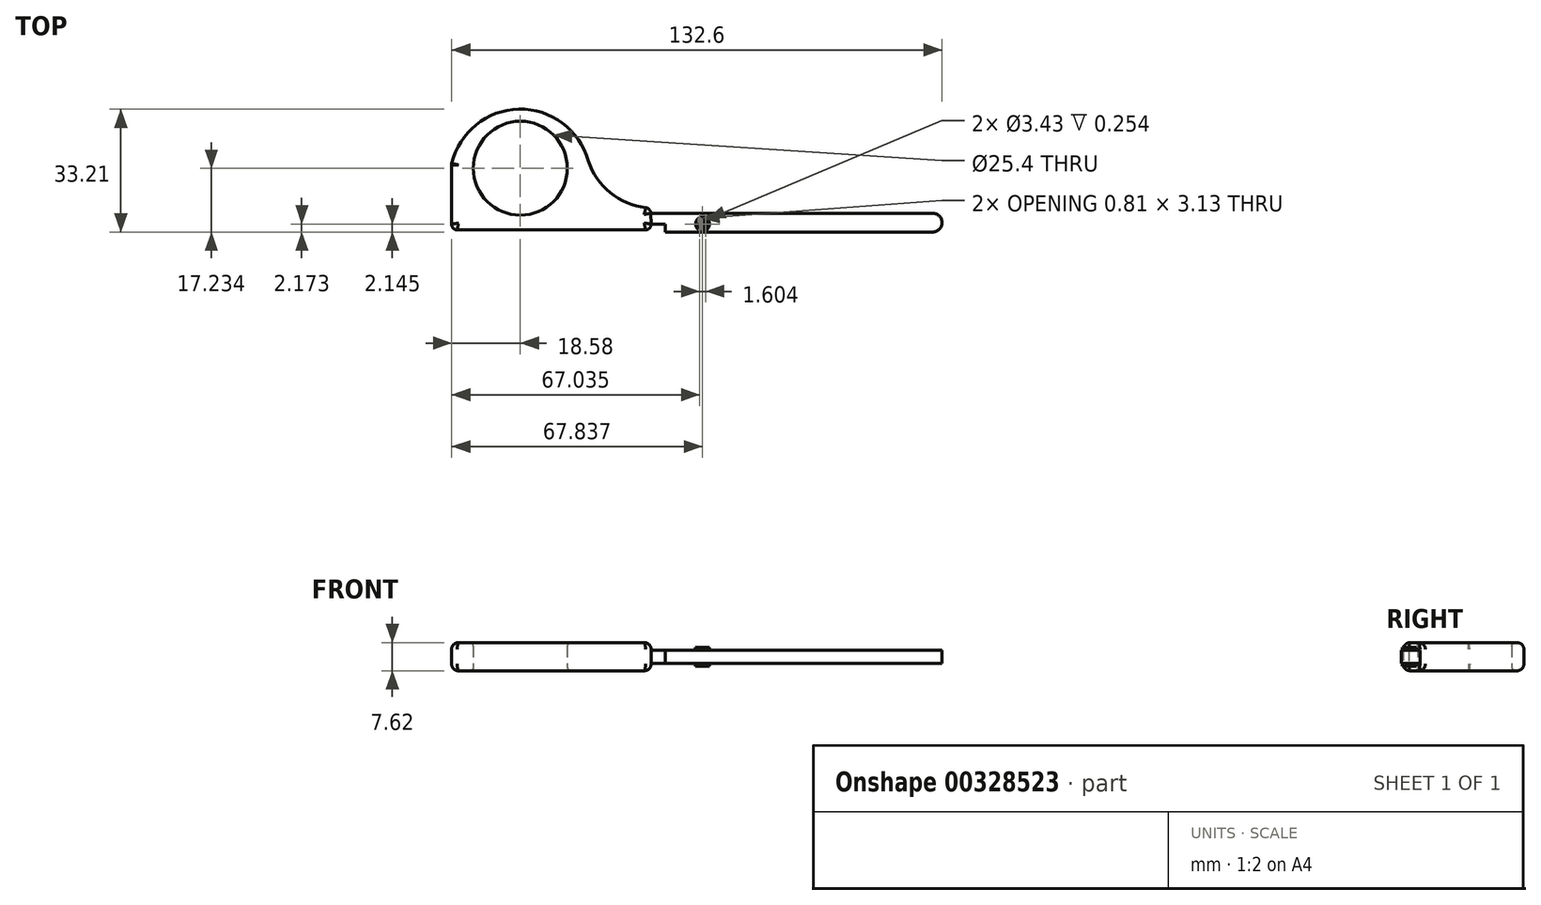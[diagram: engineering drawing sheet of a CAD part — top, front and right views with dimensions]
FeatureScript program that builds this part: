
annotation { "Feature Type Name" : "Feature", "Feature Type Description" : "" }
export const myFeature = defineFeature(function(context is Context, id is Id, definition is map)
    precondition{}
    {
        {
            var Q0;
            Q0=qCreatedBy(makeId("Top.planeOp"),FACE);
            var sketch = newSketch(context, id + "F0", { "sketchPlane" : qUnion([Q0])});
            skLineSegment(sketch, "E0", {"start": v(-56.25, 0) * mm, "end": v(-5.36, 0) * mm});
            skLineSegment(sketch, "E1", {"start": v(-57.77, 1.52) * mm, "end": v(-57.77, 17.6) * mm});
            skArc(sketch, "E2", {"start": v(-20.85, 18.71) * mm, "mid": v(-39.58, 32.62) * mm, "end": v(-57.73, 17.96) * mm});
            skArc(sketch, "E3", {"start": v(-20.82, 18.64) * mm, "mid": v(-14.89, 10.04) * mm, "end": v(-5.26, 5.97) * mm});
            skLineSegment(sketch, "E4", {"start": v(-3.91, 4.5) * mm, "end": v(-3.84, 1.56) * mm});
            skPoint(sketch, "E5.visualSharp", {"position": v(-3.95, 5.87) * mm});
            skArc(sketch, "E5.filletArc", {"start": v(-3.91, 4.5) * mm, "mid": v(-4.31, 5.49) * mm, "end": v(-5.26, 5.97) * mm});
            skPoint(sketch, "E6.visualSharp", {"position": v(-3.8, 0) * mm});
            skArc(sketch, "E6.filletArc", {"start": v(-5.36, 0) * mm, "mid": v(-4.27, 0.46) * mm, "end": v(-3.84, 1.56) * mm});
            skPoint(sketch, "E7.visualSharp", {"position": v(-57.77, 0) * mm});
            skArc(sketch, "E7.filletArc", {"start": v(-57.77, 1.52) * mm, "mid": v(-57.32, 0.45) * mm, "end": v(-56.25, 0) * mm});
            skPoint(sketch, "E8.visualSharp", {"position": v(-57.77, 17.78) * mm});
            skArc(sketch, "E8.filletArc", {"start": v(-57.73, 17.96) * mm, "mid": v(-57.76, 17.78) * mm, "end": v(-57.77, 17.6) * mm});
            skArc(sketch, "E9.filletArc", {"start": v(-20.85, 18.71) * mm, "mid": v(-20.84, 18.68) * mm, "end": v(-20.82, 18.64) * mm});
            skLineSegment(sketch, "E10", {"start": v(-3.91, 4.5) * mm, "end": v(72.29, 4.5) * mm});
            skLineSegment(sketch, "E11", {"start": v(-3.84, 1.56) * mm, "end": v(0, 1.56) * mm});
            skLineSegment(sketch, "E12", {"start": v(0, 1.56) * mm, "end": v(0, -0.58) * mm});
            skLineSegment(sketch, "E13", {"start": v(0, -0.58) * mm, "end": v(72.29, -0.58) * mm});
            skArc(sketch, "E14", {"start": v(72.29, -0.58) * mm, "mid": v(74.83, 1.96) * mm, "end": v(72.29, 4.5) * mm});
            skCircle(sketch, "E15", {"center": v(10.1, 1.56) * mm, "radius": 1.71 * mm});
            skCircle(sketch, "E16", {"center": v(-39.19, 16.65) * mm, "radius": 12.7 * mm});
            skSolve(sketch);
        }
        {
            var Q0;
            Q0=makeQuery(id+"F0.imprint","IMPRINT",FACE,{"disambiguationData":[TD([[makeQuery(id+"F0.imprint","IMPRINT",EDGE,{"derivedFrom":sQuery(id+"F0.wireOp",EDGE,"E0")}),1.0]])]});
            extrude(context, id + "F1", {"entities" : qUnion([Q0]), "endBound" : BoundingType.SYMMETRIC, "depth" : 7.62 * mm});
        }
        {
            var Q0;
            Q0=makeQuery(id+"F0.imprint","IMPRINT",FACE,{"disambiguationData":[TD([[makeQuery(id+"F0.imprint","IMPRINT",EDGE,{"derivedFrom":sQuery(id+"F0.wireOp",EDGE,"E4")}),1.0]])]});
            extrude(context, id + "F2", {"entities" : qUnion([Q0]), "operationType" : NewBodyOperationType.ADD, "endBound" : BoundingType.SYMMETRIC, "depth" : 3.56 * mm});
        }
        {
            var Q0;
            Q0=makeQuery(id+"F1.opExtrude","CAP_EDGE",EDGE,{"disambiguationData":[OSD([sQuery(id+"F0.wireOp",EDGE,"E2")])],"isStart":false});
            var Q1;
            Q1=makeQuery(id+"F1.opExtrude","CAP_EDGE",EDGE,{"disambiguationData":[OSD([sQuery(id+"F0.wireOp",EDGE,"E2")])],"isStart":true});
            var Q2;
            Q2=makeQuery(id+"F1.opExtrude","CAP_EDGE",EDGE,{"disambiguationData":[OSD([sQuery(id+"F0.wireOp",EDGE,"E3")])],"isStart":false});
            var Q3;
            Q3=makeQuery(id+"F1.opExtrude","CAP_EDGE",EDGE,{"disambiguationData":[OSD([sQuery(id+"F0.wireOp",EDGE,"E3")])],"isStart":true});
            var Q4;
            Q4=makeQuery(id+"F1.opExtrude","CAP_EDGE",EDGE,{"disambiguationData":[OSD([sQuery(id+"F0.wireOp",EDGE,"E8.filletArc")])],"isStart":false});
            var Q5;
            Q5=makeQuery(id+"F1.opExtrude","CAP_EDGE",EDGE,{"disambiguationData":[OSD([sQuery(id+"F0.wireOp",EDGE,"E8.filletArc")])],"isStart":true});
            var Q6;
            Q6=makeQuery(id+"F1.opExtrude","CAP_EDGE",EDGE,{"disambiguationData":[OSD([sQuery(id+"F0.wireOp",EDGE,"E1")])],"isStart":true});
            var Q7;
            Q7=makeQuery(id+"F1.opExtrude","CAP_EDGE",EDGE,{"disambiguationData":[OSD([sQuery(id+"F0.wireOp",EDGE,"E1")])],"isStart":false});
            var Q8;
            Q8=makeQuery(id+"F1.opExtrude","CAP_EDGE",EDGE,{"disambiguationData":[OSD([sQuery(id+"F0.wireOp",EDGE,"E7.filletArc")])],"isStart":false});
            var Q9;
            Q9=makeQuery(id+"F1.opExtrude","CAP_EDGE",EDGE,{"disambiguationData":[OSD([sQuery(id+"F0.wireOp",EDGE,"E0")])],"isStart":false});
            var Q10;
            Q10=makeQuery(id+"F1.opExtrude","CAP_EDGE",EDGE,{"disambiguationData":[OSD([sQuery(id+"F0.wireOp",EDGE,"E7.filletArc")])],"isStart":true});
            var Q11;
            Q11=makeQuery(id+"F1.opExtrude","CAP_EDGE",EDGE,{"disambiguationData":[OSD([sQuery(id+"F0.wireOp",EDGE,"E0")])],"isStart":true});
            var Q12;
            Q12=makeQuery(id+"F1.opExtrude","CAP_EDGE",EDGE,{"disambiguationData":[OSD([sQuery(id+"F0.wireOp",EDGE,"MBKP8UZo-nLue-SihB-gih0-BUNX2vB4kbxo")])],"isStart":false});
            var Q13;
            Q13=makeQuery(id+"F1.opExtrude","CAP_EDGE",EDGE,{"disambiguationData":[OSD([sQuery(id+"F0.wireOp",EDGE,"MBKP8UZo-nLue-SihB-gih0-BUNX2vB4kbxo")])],"isStart":true});
            var Q14;
            Q14=makeQuery(id+"F1.opExtrude","CAP_EDGE",EDGE,{"disambiguationData":[OSD([sQuery(id+"F0.wireOp",EDGE,"E5.filletArc")])],"isStart":false});
            var Q15;
            Q15=makeQuery(id+"F1.opExtrude","CAP_EDGE",EDGE,{"disambiguationData":[OSD([sQuery(id+"F0.wireOp",EDGE,"E4")])],"isStart":false});
            var Q16;
            Q16=makeQuery(id+"F1.opExtrude","CAP_EDGE",EDGE,{"disambiguationData":[OSD([sQuery(id+"F0.wireOp",EDGE,"E6.filletArc")])],"isStart":false});
            var Q17;
            Q17=makeQuery(id+"F1.opExtrude","CAP_EDGE",EDGE,{"disambiguationData":[OSD([sQuery(id+"F0.wireOp",EDGE,"E4")])],"isStart":true});
            var Q18;
            Q18=makeQuery(id+"F1.opExtrude","CAP_EDGE",EDGE,{"disambiguationData":[OSD([sQuery(id+"F0.wireOp",EDGE,"E6.filletArc")])],"isStart":true});
            var Q19;
            Q19=makeQuery(id+"F1.opExtrude","CAP_EDGE",EDGE,{"disambiguationData":[OSD([sQuery(id+"F0.wireOp",EDGE,"E5.filletArc")])],"isStart":true});
            fillet(context, id + "F3", {"entities" : qUnion([Q0, Q1, Q2, Q3, Q4, Q5, Q6, Q7, Q8, Q9, Q10, Q11, Q12, Q13, Q14, Q15, Q16, Q17, Q18, Q19]), "radius" : 1.84 * mm, "tangentPropagation" : true, "allowEdgeOverflow" : false});
        }
        {
            var Q0;
            Q0=makeQuery(id+"F1.opExtrude","CAP_EDGE",EDGE,{"disambiguationData":[OSD([sQuery(id+"F0.wireOp",EDGE,"E16")])],"isStart":true});
            var Q1;
            Q1=makeQuery(id+"F1.opExtrude","CAP_EDGE",EDGE,{"disambiguationData":[OSD([sQuery(id+"F0.wireOp",EDGE,"E16")])],"isStart":false});
            fillet(context, id + "F4", {"entities" : qUnion([Q0, Q1]), "radius" : 0.98 * mm, "tangentPropagation" : true, "allowEdgeOverflow" : false});
        }
        {
            var Q0;
            Q0=qCreatedBy(makeId("Top.planeOp"),FACE);
            var sketch = newSketch(context, id + "F5", { "sketchPlane" : qUnion([Q0])});
            skCircle(sketch, "E17", {"center": v(10.07, 1.6) * mm, "radius": 1.71 * mm});
            skLineSegment(sketch, "E18", {"start": v(9.67, 3.13) * mm, "end": v(9.67, 0) * mm});
            skLineSegment(sketch, "E19", {"start": v(10.07, 1.6) * mm, "end": v(10.07, -15.89) * mm, "construction": true});
            skLineSegment(sketch, "E20", {"start": v(10.07, -15.89) * mm, "end": v(10.07, 1.6) * mm, "construction": true});
            skLineSegment(sketch, "E21", {"start": v(10.07, 1.6) * mm, "end": v(10.07, 12.33) * mm, "construction": true});
            skLineSegment(sketch, "E22.MirrorCS", {"start": v(10.46, 3.13) * mm, "end": v(10.46, 0) * mm});
            skArc(sketch, "E23", {"start": v(9.67, 3.13) * mm, "mid": v(8.86, 1.56) * mm, "end": v(9.67, 0) * mm});
            skArc(sketch, "E24.MirrorCS", {"start": v(10.46, 3.13) * mm, "mid": v(11.27, 1.56) * mm, "end": v(10.46, 0) * mm});
            skCircle(sketch, "E25", {"center": v(10.07, 1.6) * mm, "radius": 1.89 * mm});
            skSolve(sketch);
        }
        {
            var Q0;
            Q0=makeQuery(id+"F5.imprint","IMPRINT",FACE,{"disambiguationData":[TD([[makeQuery(id+"F5.imprint","IMPRINT",EDGE,{"derivedFrom":sQuery(id+"F5.wireOp",EDGE,"E17")}),1.0]])]});
            extrude(context, id + "F6", {"entities" : qUnion([Q0]), "operationType" : NewBodyOperationType.ADD, "endBound" : BoundingType.SYMMETRIC, "depth" : 4.57 * mm});
        }
        {
            var Q0;
            Q0=makeQuery(id+"F5.imprint","IMPRINT",FACE,{"disambiguationData":[TD([[makeQuery(id+"F5.imprint","IMPRINT",EDGE,{"derivedFrom":sQuery(id+"F5.wireOp",EDGE,"E18")}),-1.0]])]});
            var Q1;
            Q1=makeQuery(id+"F5.imprint","IMPRINT",FACE,{"disambiguationData":[TD([[makeQuery(id+"F5.imprint","IMPRINT",EDGE,{"derivedFrom":sQuery(id+"F5.wireOp",EDGE,"E22.MirrorCS")}),1.0]])]});
            extrude(context, id + "F7", {"entities" : qUnion([Q0, Q1]), "operationType" : NewBodyOperationType.ADD, "endBound" : BoundingType.SYMMETRIC, "depth" : 4.95 * mm});
        }
        {
            var Q0;
            Q0=makeQuery(id+"F5.imprint","IMPRINT",FACE,{"disambiguationData":[TD([[makeQuery(id+"F5.imprint","IMPRINT",EDGE,{"derivedFrom":sQuery(id+"F5.wireOp",EDGE,"E17")}),-1.0]])]});
            extrude(context, id + "F8", {"entities" : qUnion([Q0]), "operationType" : NewBodyOperationType.ADD, "endBound" : BoundingType.SYMMETRIC, "depth" : 5.08 * mm});
        }
    });
